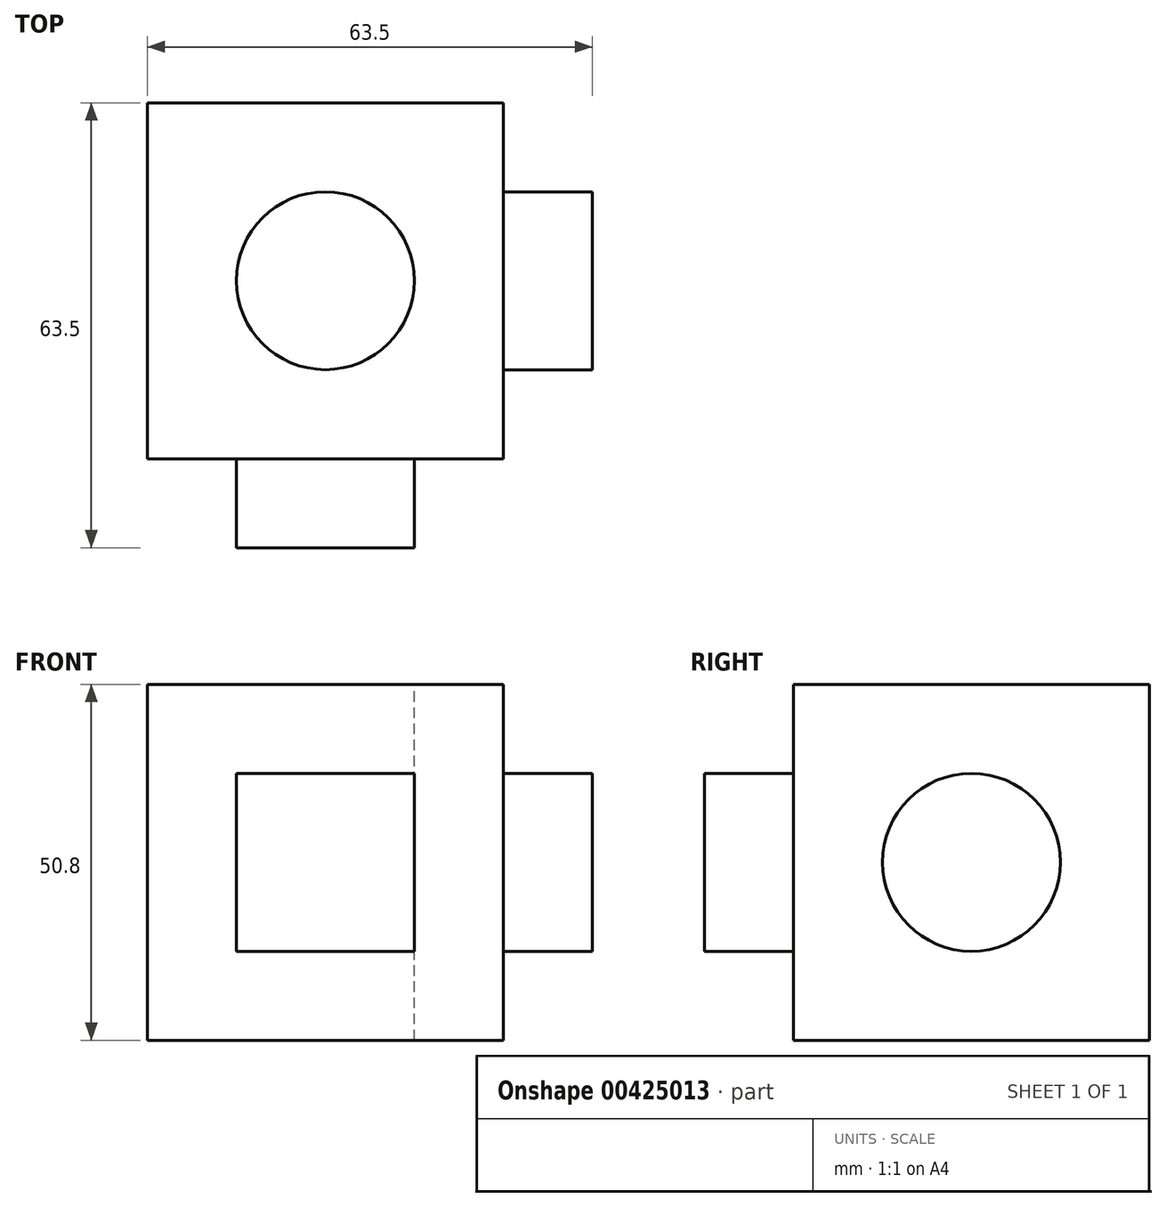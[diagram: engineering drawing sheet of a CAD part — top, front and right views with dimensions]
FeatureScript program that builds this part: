
annotation { "Feature Type Name" : "Feature", "Feature Type Description" : "" }
export const myFeature = defineFeature(function(context is Context, id is Id, definition is map)
    precondition{}
    {
        {
            var Q0;
            Q0=qCreatedBy(makeId("Front.planeOp"),FACE);
            var sketch = newSketch(context, id + "F0", { "sketchPlane" : qUnion([Q0])});
            skLineSegment(sketch, "E0.bottom", {"start": v(0, 0) * mm, "end": v(-50.8, 0) * mm});
            skLineSegment(sketch, "E0.top", {"start": v(0, 50.8) * mm, "end": v(-50.8, 50.8) * mm});
            skLineSegment(sketch, "E0.left", {"start": v(0, 0) * mm, "end": v(0, 50.8) * mm});
            skLineSegment(sketch, "E0.right", {"start": v(-50.8, 0) * mm, "end": v(-50.8, 50.8) * mm});
            skSolve(sketch);
        }
        {
            var Q0;
            Q0=makeQuery(id+"F0.imprint","IMPRINT",FACE,{"disambiguationData":[TD([[makeQuery(id+"F0.imprint","IMPRINT",EDGE,{"derivedFrom":sQuery(id+"F0.wireOp",EDGE,"E0.bottom")}),-1.0]])]});
            extrude(context, id + "F1", {"entities" : qUnion([Q0]), "depth" : 50.8 * mm});
        }
        {
            var Q0;
            Q0=makeQuery(id+"F1.opExtrude","SWEPT_FACE",FACE,{"disambiguationData":[OSD([sQuery(id+"F0.wireOp",EDGE,"E0.top")])]});
            var sketch = newSketch(context, id + "F2", { "sketchPlane" : qUnion([Q0])});
            skCircle(sketch, "E1", {"center": v(-25.4, -25.4) * mm, "radius": 12.7 * mm});
            skSolve(sketch);
        }
        {
            var Q0;
            Q0=makeQuery(id+"F2.imprint","IMPRINT",FACE,{"disambiguationData":[TD([[makeQuery(id+"F2.imprint","IMPRINT",EDGE,{"derivedFrom":sQuery(id+"F2.wireOp",EDGE,"E1")}),1.0]])]});
            extrude(context, id + "F3", {"entities" : qUnion([Q0]), "operationType" : NewBodyOperationType.REMOVE, "oppositeDirection" : true, "depth" : 83.06 * mm});
        }
        {
            var Q0;
            Q0=makeQuery(id+"F1.opExtrude","CAP_FACE",FACE,{"disambiguationData":[OSD([sQuery(id+"F0.wireOp",EDGE,"E0.bottom"),sQuery(id+"F0.wireOp",EDGE,"E0.top"),sQuery(id+"F0.wireOp",EDGE,"E0.left"),sQuery(id+"F0.wireOp",EDGE,"E0.right")])],"isStart":false});
            var sketch = newSketch(context, id + "F4", { "sketchPlane" : qUnion([Q0])});
            skLineSegment(sketch, "E2.bottom", {"start": v(-38.1, 38.1) * mm, "end": v(-12.7, 38.1) * mm});
            skLineSegment(sketch, "E2.top", {"start": v(-38.1, 12.7) * mm, "end": v(-12.7, 12.7) * mm});
            skLineSegment(sketch, "E2.left", {"start": v(-38.1, 38.1) * mm, "end": v(-38.1, 12.7) * mm});
            skLineSegment(sketch, "E2.right", {"start": v(-12.7, 38.1) * mm, "end": v(-12.7, 12.7) * mm});
            skSolve(sketch);
        }
        {
            var Q0;
            Q0=makeQuery(id+"F4.imprint","IMPRINT",FACE,{"disambiguationData":[TD([[makeQuery(id+"F4.imprint","IMPRINT",EDGE,{"derivedFrom":sQuery(id+"F4.wireOp",EDGE,"E2.bottom")}),-1.0]])]});
            extrude(context, id + "F5", {"entities" : qUnion([Q0]), "operationType" : NewBodyOperationType.ADD, "depth" : 12.7 * mm});
        }
        {
            var Q0;
            Q0=makeQuery(id+"F1.opExtrude","SWEPT_FACE",FACE,{"disambiguationData":[OSD([sQuery(id+"F0.wireOp",EDGE,"E0.left")])]});
            var sketch = newSketch(context, id + "F6", { "sketchPlane" : qUnion([Q0])});
            skCircle(sketch, "E3", {"center": v(-25.4, 25.4) * mm, "radius": 12.7 * mm});
            skSolve(sketch);
        }
        {
            var Q0;
            Q0=makeQuery(id+"F6.imprint","IMPRINT",FACE,{"disambiguationData":[TD([[makeQuery(id+"F6.imprint","IMPRINT",EDGE,{"derivedFrom":sQuery(id+"F6.wireOp",EDGE,"E3")}),1.0]])]});
            extrude(context, id + "F7", {"entities" : qUnion([Q0]), "operationType" : NewBodyOperationType.ADD, "depth" : 12.7 * mm});
        }
    });
